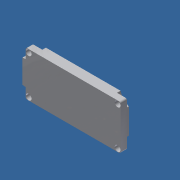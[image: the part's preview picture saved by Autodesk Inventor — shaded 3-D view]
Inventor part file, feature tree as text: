
AUTODESK INVENTOR PART (.ipt)
format: ipt  version: 2014 (Build 180170000, 170)  size: 463,360 bytes
history: native  units: in
note: dims shown in document units (in); Inventor stores cm internally (conversion verified against a paired STEP export)
features: projected_geometry x7, sketch x4, extrude x3, reference x3, imported_body x1, boolean_combine x1, plane x1
ambient origin geometry x8: Origin, YZ Plane, XZ Plane, XY Plane, X Axis, Y Axis, Z Axis, Center Point
bodies: Solid1 (feature_tree), Solid3 (feature_tree), Solid4 (feature_tree), Solid2 (feature_tree)
feature tree (20):
  extrude  "Extrusion1"  Depth=0.1181in
  imported_body  "Base1"
  boolean_combine  "Combine1"
  plane  "Work Plane1"
  extrude  "Extrusion2"  Depth=0.1181in
  sketch  "Sketch3"  dims[d4=0.5118in d5=0.0in d6=0.0591in]
  extrude  "Extrusion3"  Depth=0.0591in
  sketch  "Sketch1"  dims[d0=0.1181in d1=0.1181in]
  reference  "Reference1"
  reference  "Reference2"
  reference  "Reference3"
  sketch  "Sketch2"  dims[d2=0.1181in d3=0.1181in]
  projected_geometry  "Projected Loop1"
  projected_geometry  "Projected Loop2"
  sketch  "Sketch4"  dims[d7=0.0591in d8=0.0in d9=0.0512in d10=0.0906in d11=0.0906in d12=0.0906in d13=0.0906in d14=0.0984in d15=0.0in]
  projected_geometry  "Projected Loop3"
  projected_geometry  "Projected Loop4"
  projected_geometry  "Projected Loop5"
  projected_geometry  "Projected Loop6"
  projected_geometry  "Projected Loop7"
